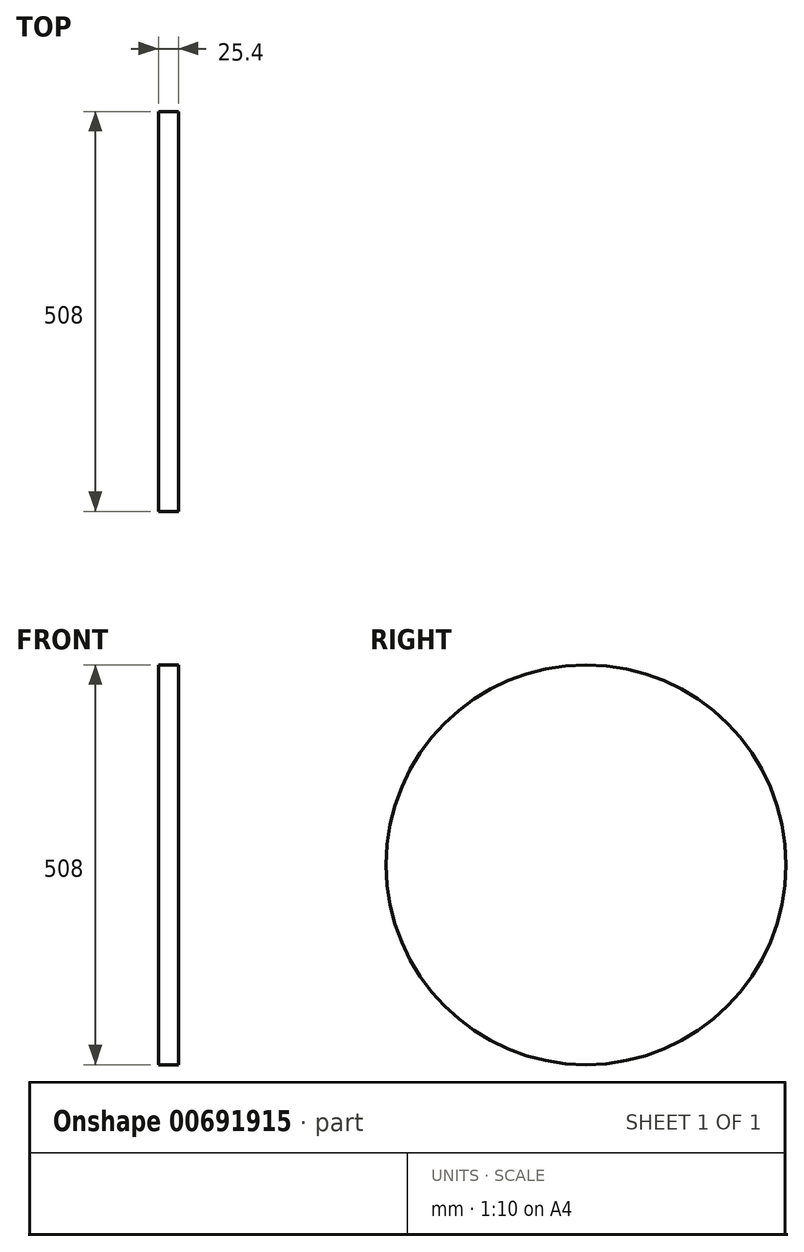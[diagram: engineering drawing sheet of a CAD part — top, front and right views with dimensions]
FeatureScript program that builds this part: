
annotation { "Feature Type Name" : "Feature", "Feature Type Description" : "" }
export const myFeature = defineFeature(function(context is Context, id is Id, definition is map)
    precondition{}
    {
        {
            var Q0;
            Q0=qCreatedBy(makeId("Right.planeOp"),FACE);
            var sketch = newSketch(context, id + "F0", { "sketchPlane" : qUnion([Q0])});
            skCircle(sketch, "E0", {"center": v(0, 0) * mm, "radius": 254 * mm});
            skSolve(sketch);
        }
        {
            var Q0;
            Q0 = qSketchRegion(id + "F0", true);
            extrude(context, id + "F1", {"entities" : qUnion([Q0]), "endBound" : BoundingType.SYMMETRIC, "depth" : 25.4 * mm, "offsetDistance" : 25.4 * mm});
        }
    });
